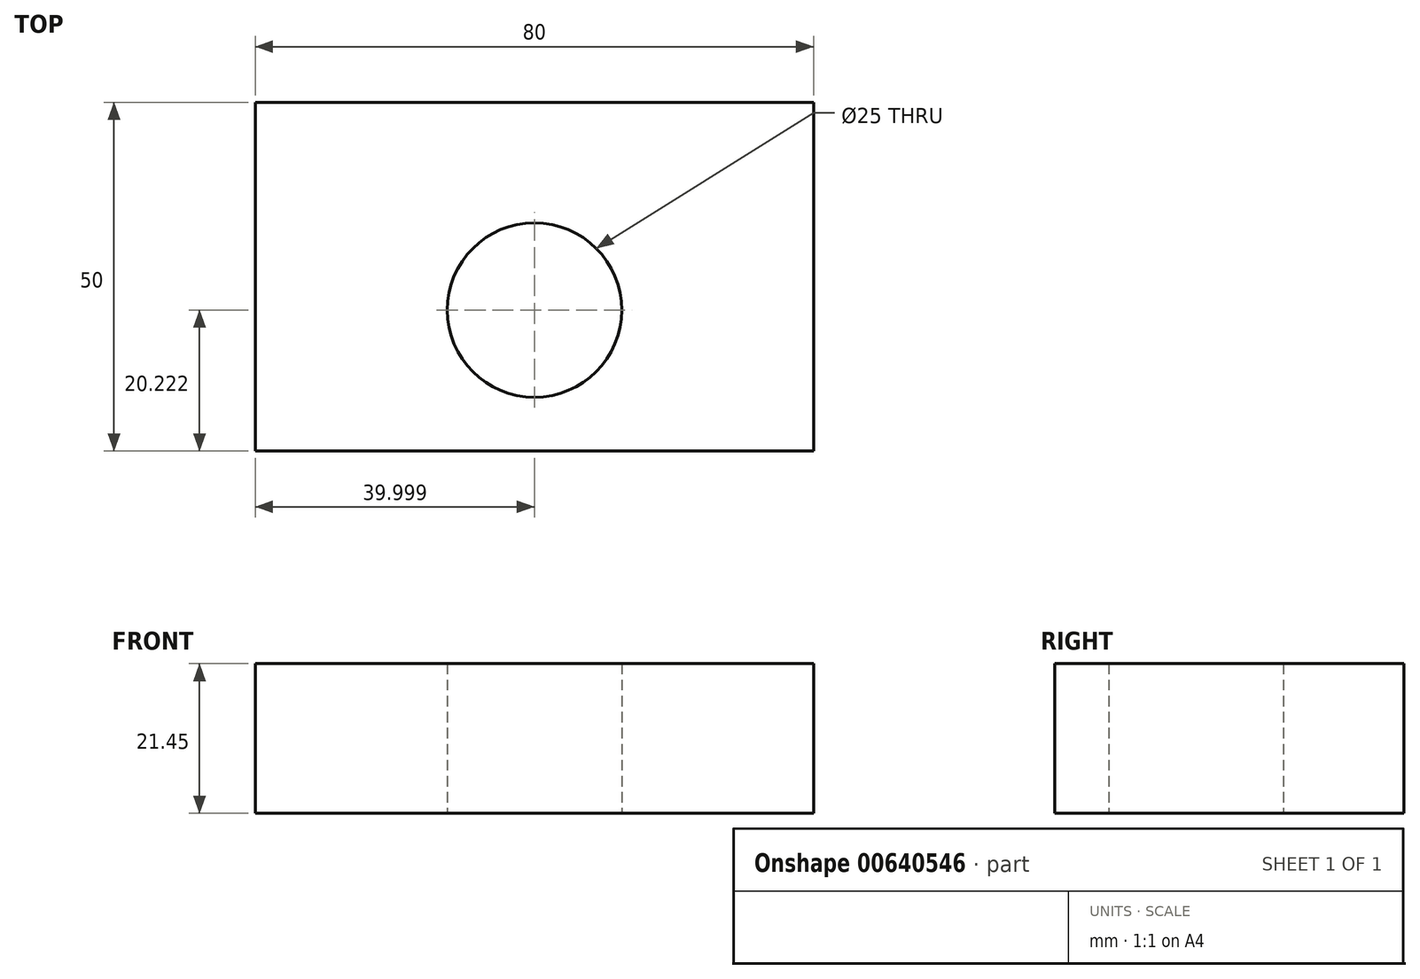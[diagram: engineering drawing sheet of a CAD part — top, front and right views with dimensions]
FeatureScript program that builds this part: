
annotation { "Feature Type Name" : "Feature", "Feature Type Description" : "" }
export const myFeature = defineFeature(function(context is Context, id is Id, definition is map)
    precondition{}
    {
        {
            var Q0;
            Q0=qCreatedBy(makeId("Front.planeOp"),FACE);
            var sketch = newSketch(context, id + "F0", { "sketchPlane" : qUnion([Q0])});
            skLineSegment(sketch, "E0.bottom", {"start": v(-17.76, 30) * mm, "end": v(62.24, 30) * mm});
            skLineSegment(sketch, "E0.top", {"start": v(-17.76, 8.55) * mm, "end": v(62.24, 8.55) * mm});
            skLineSegment(sketch, "E0.left", {"start": v(-17.76, 30) * mm, "end": v(-17.76, 8.55) * mm});
            skLineSegment(sketch, "E0.right", {"start": v(62.24, 30) * mm, "end": v(62.24, 8.55) * mm});
            skSolve(sketch);
        }
        {
            var Q0;
            Q0 = qSketchRegion(id + "F0", true);
            extrude(context, id + "F1", {"entities" : qUnion([Q0]), "endBound" : BoundingType.SYMMETRIC, "depth" : 50 * mm, "offsetDistance" : 25 * mm});
        }
        {
            var Q0;
            Q0=makeQuery(id+"F1.opExtrude","SWEPT_FACE",FACE,{"disambiguationData":[OSD([sQuery(id+"F0.wireOp",EDGE,"E0.top")])]});
            var sketch = newSketch(context, id + "F2", { "sketchPlane" : qUnion([Q0])});
            skCircle(sketch, "E1", {"center": v(22.24, 4.78) * mm, "radius": 12.5 * mm});
            skSolve(sketch);
        }
        {
            var Q0;
            Q0=makeQuery(id+"F2.imprint","IMPRINT",FACE,{"disambiguationData":[TD([[makeQuery(id+"F2.imprint","IMPRINT",EDGE,{"derivedFrom":sQuery(id+"F2.wireOp",EDGE,"E1")}),1.0]])]});
            extrude(context, id + "F3", {"entities" : qUnion([Q0]), "operationType" : NewBodyOperationType.REMOVE, "endBound" : BoundingType.UP_TO_NEXT, "oppositeDirection" : true, "depth" : 72 * mm, "offsetDistance" : 25 * mm});
        }
    });
